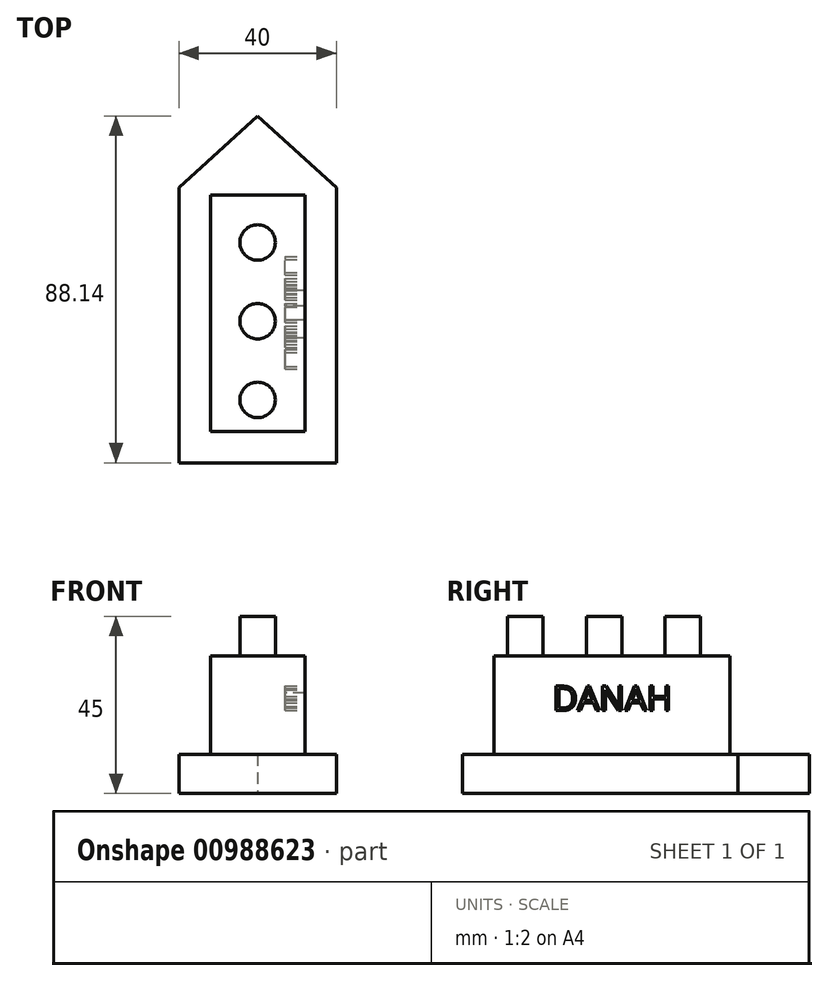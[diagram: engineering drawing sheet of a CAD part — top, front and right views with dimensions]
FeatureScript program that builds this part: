
annotation { "Feature Type Name" : "Feature", "Feature Type Description" : "" }
export const myFeature = defineFeature(function(context is Context, id is Id, definition is map)
    precondition{}
    {
        {
            var Q0;
            Q0=qCreatedBy(makeId("Top.planeOp"),FACE);
            var sketch = newSketch(context, id + "F0", { "sketchPlane" : qUnion([Q0])});
            skLineSegment(sketch, "E0", {"start": v(-20, 23.4) * mm, "end": v(-20, -46.6) * mm});
            skLineSegment(sketch, "E1", {"start": v(-20, 23.4) * mm, "end": v(0, 41.53) * mm});
            skLineSegment(sketch, "E2", {"start": v(0, 41.53) * mm, "end": v(20, 23.4) * mm});
            skLineSegment(sketch, "E3", {"start": v(20, 23.4) * mm, "end": v(20, -46.6) * mm});
            skLineSegment(sketch, "E4", {"start": v(20, -46.6) * mm, "end": v(-20, -46.6) * mm});
            skSolve(sketch);
        }
        {
            var Q0;
            Q0=makeQuery(id+"F0.imprint","IMPRINT",FACE,{"disambiguationData":[TD([[makeQuery(id+"F0.imprint","IMPRINT",EDGE,{"derivedFrom":sQuery(id+"F0.wireOp",EDGE,"E0")}),1.0]])]});
            extrude(context, id + "F1", {"entities" : qUnion([Q0]), "depth" : 10 * mm, "offsetDistance" : 25 * mm});
        }
        {
            var Q0;
            Q0=makeQuery(id+"F1.opExtrude","CAP_FACE",FACE,{"disambiguationData":[OSD([sQuery(id+"F0.wireOp",EDGE,"E0"),sQuery(id+"F0.wireOp",EDGE,"E1"),sQuery(id+"F0.wireOp",EDGE,"E2"),sQuery(id+"F0.wireOp",EDGE,"E3"),sQuery(id+"F0.wireOp",EDGE,"E4")])],"isStart":false});
            var sketch = newSketch(context, id + "F2", { "sketchPlane" : qUnion([Q0])});
            skLineSegment(sketch, "E5", {"start": v(-12, 21.4) * mm, "end": v(-12, -38.6) * mm});
            skLineSegment(sketch, "E6", {"start": v(-12, -38.6) * mm, "end": v(12, -38.6) * mm});
            skLineSegment(sketch, "E7", {"start": v(12, -38.6) * mm, "end": v(12, 21.4) * mm});
            skLineSegment(sketch, "E8", {"start": v(12, 21.4) * mm, "end": v(-12, 21.4) * mm});
            skSolve(sketch);
        }
        {
            var Q0;
            Q0=makeQuery(id+"F2.imprint","IMPRINT",FACE,{"disambiguationData":[TD([[makeQuery(id+"F2.imprint","IMPRINT",EDGE,{"derivedFrom":sQuery(id+"F2.wireOp",EDGE,"E5")}),1.0]])]});
            extrude(context, id + "F3", {"entities" : qUnion([Q0]), "operationType" : NewBodyOperationType.ADD, "depth" : 25 * mm, "offsetDistance" : 25 * mm});
        }
        {
            var Q0;
            Q0=makeQuery(id+"F3.opExtrude","CAP_FACE",FACE,{"disambiguationData":[OSD([sQuery(id+"F2.wireOp",EDGE,"E5"),sQuery(id+"F2.wireOp",EDGE,"E6"),sQuery(id+"F2.wireOp",EDGE,"E7"),sQuery(id+"F2.wireOp",EDGE,"E8")])],"isStart":false});
            var sketch = newSketch(context, id + "F4", { "sketchPlane" : qUnion([Q0])});
            skCircle(sketch, "E9", {"center": v(0, 9.4) * mm, "radius": 4.5 * mm});
            skCircle(sketch, "E10", {"center": v(0, -10.6) * mm, "radius": 4.5 * mm});
            skCircle(sketch, "E11", {"center": v(0, -30.6) * mm, "radius": 4.5 * mm});
            skSolve(sketch);
        }
        {
            var Q0;
            Q0 = qSketchRegion(id + "F4", true);
            extrude(context, id + "F5", {"entities" : qUnion([Q0]), "operationType" : NewBodyOperationType.ADD, "depth" : 10 * mm, "offsetDistance" : 25 * mm});
        }
        {
            var Q0;
            Q0=makeQuery(id+"F3.opExtrude","SWEPT_FACE",FACE,{"disambiguationData":[OSD([sQuery(id+"F2.wireOp",EDGE,"E7")])]});
            var sketch = newSketch(context, id + "F6", { "sketchPlane" : qUnion([Q0])});
            skText(sketch, "E12", { "text": "DANAH\n", "fontName": "OpenSans-Regular.ttf"});
            const initialGuessF6  = {"E12": [-0.02364, 0.02108, 1, 0, 0.00625]};
            skSetInitialGuess(sketch, initialGuessF6);
            skSolve(sketch);
        }
        {
            var Q0;
            Q0 = qSketchRegion(id + "F6", true);
            extrude(context, id + "F7", {"entities" : qUnion([Q0]), "operationType" : NewBodyOperationType.REMOVE, "oppositeDirection" : true, "depth" : 5 * mm, "offsetDistance" : 25 * mm});
        }
    });
